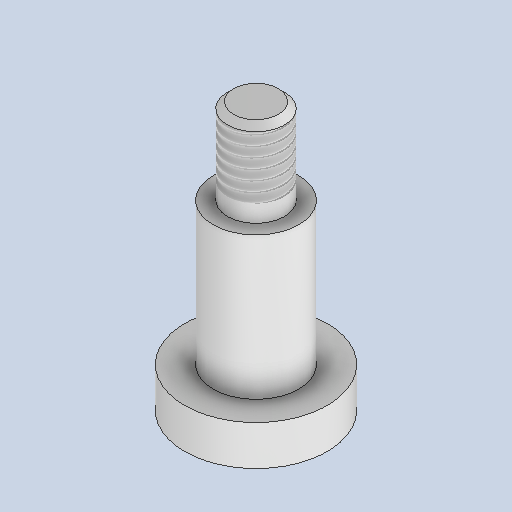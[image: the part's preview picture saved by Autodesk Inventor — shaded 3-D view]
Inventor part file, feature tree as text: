
AUTODESK INVENTOR PART (.ipt)
format: ipt  version: 2024.2 (Build 282272000, 272)  size: 289,792 bytes
history: native  units: mm
features: sketch x2, revolve x1, thread x1, extrude x1, chamfer x1
ambient origin geometry x8: Origin, YZ Plane, XZ Plane, XY Plane, X Axis, Y Axis, Z Axis, Center Point
bodies: Solid1 (feature_tree)
feature tree (6):
  revolve  "Revolution1"  [1 undecoded]
  thread  "Thread1"  [1 undecoded]
  extrude  "Extrusion1"  Depth=10.0mm
  chamfer  "Chamfer1"  Distance=2.8mm
  sketch  "Sketch1"  dims[d0=10.0mm d1=6.0mm d2=4.0mm]
  sketch  "Sketch2"  dims[d3=6.0mm d4=10.0mm d5=2.8mm d6=90.0deg d7=6.0mm d8=1.2mm d9=2.5mm d10=2.0mm d11=0.0mm d12=0.43mm d13=2.0mm d14=45.0deg]
note: 2 required parameter values undecoded (feature->parameter linkage not recoverable at this tier; creation-order binding heuristic only, values carry confidence <= 0.55)